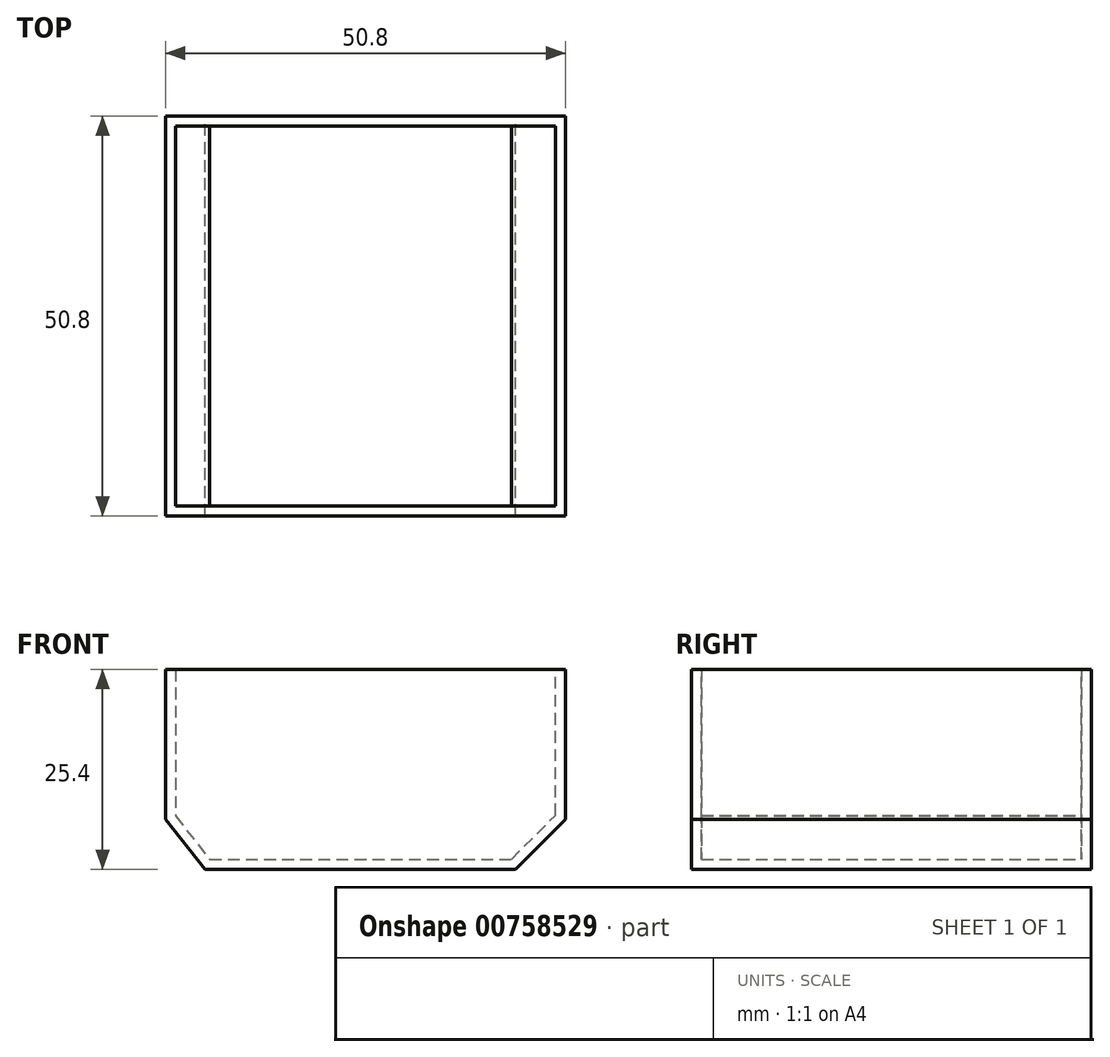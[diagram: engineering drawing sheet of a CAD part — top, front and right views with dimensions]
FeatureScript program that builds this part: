
annotation { "Feature Type Name" : "Feature", "Feature Type Description" : "" }
export const myFeature = defineFeature(function(context is Context, id is Id, definition is map)
    precondition{}
    {
        {
            var Q0;
            Q0=qCreatedBy(makeId("Front.planeOp"),FACE);
            var sketch = newSketch(context, id + "F0", { "sketchPlane" : qUnion([Q0])});
            skLineSegment(sketch, "E0", {"start": v(-25.4, 19.05) * mm, "end": v(-25.4, 0) * mm});
            skLineSegment(sketch, "E1", {"start": v(-25.4, 0) * mm, "end": v(-20.4, -6.35) * mm});
            skLineSegment(sketch, "E2", {"start": v(-20.4, -6.35) * mm, "end": v(0, -6.35) * mm});
            skLineSegment(sketch, "E3", {"start": v(0, -6.35) * mm, "end": v(19.04, -6.35) * mm});
            skLineSegment(sketch, "E4", {"start": v(19.04, -6.35) * mm, "end": v(25.4, 0) * mm});
            skLineSegment(sketch, "E5", {"start": v(25.4, 0) * mm, "end": v(25.4, 19.05) * mm});
            skLineSegment(sketch, "E6", {"start": v(25.4, 19.05) * mm, "end": v(-25.4, 19.05) * mm});
            skLineSegment(sketch, "E7", {"start": v(0, 19.05) * mm, "end": v(0, -6.35) * mm});
            skSolve(sketch);
        }
        {
            var Q0;
            {var subQ1=sQuery(id+"F0.wireOp",EDGE,"E0");Q0=makeQuery(id+"F0.imprint","IMPRINT",FACE,{"disambiguationData":[TD([[makeQuery(id+"F0.imprint","IMPRINT",EDGE,{"derivedFrom":subQ1}),1.0]])]});}
            var Q1;
            Q1=makeQuery(id+"F0.imprint","IMPRINT",FACE,{"disambiguationData":[TD([[makeQuery(id+"F0.imprint","IMPRINT",EDGE,{"derivedFrom":sQuery(id+"F0.wireOp",EDGE,"E3")}),1.0]])]});
            extrude(context, id + "F1", {"entities" : qUnion([Q0, Q1]), "depth" : 50.8 * mm, "offsetDistance" : 25.4 * mm});
        }
        {
            var Q0;
            Q0=makeQuery(id+"F1.opExtrude","SWEPT_FACE",FACE,{"disambiguationData":[OSD([sQuery(id+"F0.wireOp",EDGE,"E6")])]});
            shell(context, id + "F2", {"entities" : qUnion([Q0]), "thickness" : 1.27 * mm});
        }
    });
